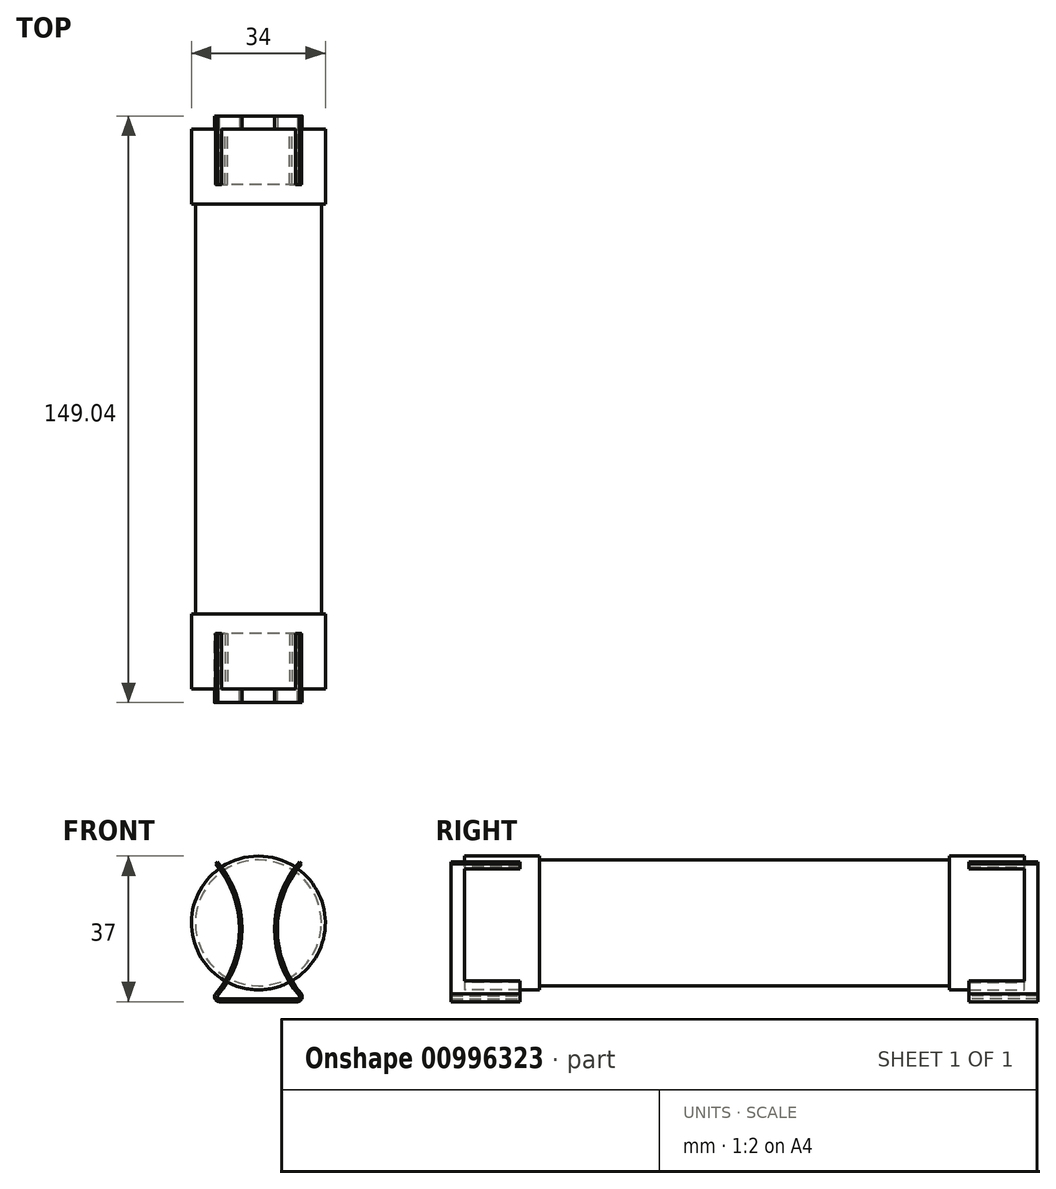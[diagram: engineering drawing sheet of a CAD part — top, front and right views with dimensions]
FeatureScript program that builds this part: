
annotation { "Feature Type Name" : "Feature", "Feature Type Description" : "" }
export const myFeature = defineFeature(function(context is Context, id is Id, definition is map)
    precondition{}
    {
        {
            var Q0;
            Q0=qCreatedBy(makeId("Front.planeOp"),FACE);
            var sketch = newSketch(context, id + "F0", { "sketchPlane" : qUnion([Q0])});
            skArc(sketch, "E0", {"start": v(-19.83, 17) * mm, "mid": v(-26.12, 0) * mm, "end": v(-19.83, -17) * mm});
            skArc(sketch, "E1", {"start": v(-19.3, 16.5) * mm, "mid": v(-25.4, 0) * mm, "end": v(-19.3, -16.5) * mm});
            skLineSegment(sketch, "E2", {"start": v(0, 0) * mm, "end": v(-25.4, 0) * mm, "construction": true});
            skLineSegment(sketch, "E3", {"start": v(-25.4, 0) * mm, "end": v(-19.3, 16.5) * mm, "construction": true});
            skLineSegment(sketch, "E4.MirrorCS", {"start": v(-25.4, 0) * mm, "end": v(-19.3, -16.5) * mm, "construction": true});
            skPoint(sketch, "E5", {"position": v(-26.12, 0) * mm});
            skLineSegment(sketch, "E6", {"start": v(-26.12, 0) * mm, "end": v(-19.83, 17) * mm, "construction": true});
            skLineSegment(sketch, "E7.MirrorCS", {"start": v(-26.12, 0) * mm, "end": v(-19.83, -17) * mm, "construction": true});
            skLineSegment(sketch, "E8", {"start": v(-19.83, -17) * mm, "end": v(-19.3, -16.5) * mm});
            skLineSegment(sketch, "E9", {"start": v(-19.83, 17) * mm, "end": v(-19.3, 16.5) * mm});
            skArc(sketch, "E10.filletArc", {"start": v(-20.29, -17.7) * mm, "mid": v(-19.87, -17.47) * mm, "end": v(-19.83, -17) * mm});
            skArc(sketch, "E11", {"start": v(-20.29, -18.47) * mm, "mid": v(-19.21, -17.78) * mm, "end": v(-19.3, -16.5) * mm});
            skLineSegment(sketch, "E12", {"start": v(-20.29, -17.7) * mm, "end": v(-40.18, -17.7) * mm});
            skLineSegment(sketch, "E13", {"start": v(-20.29, -18.47) * mm, "end": v(-40.18, -18.47) * mm});
            skLineSegment(sketch, "E14", {"start": v(-40.18, -18.47) * mm, "end": v(-40.18, -17.7) * mm});
            skLineSegment(sketch, "E15", {"start": v(-30.23, -17.7) * mm, "end": v(-30.23, -16.44) * mm, "construction": true});
            skLineSegment(sketch, "E16.MirrorCS", {"start": v(-40.63, -17) * mm, "end": v(-41.16, -16.5) * mm});
            skArc(sketch, "E17.MirrorCS", {"start": v(-40.18, -18.47) * mm, "mid": v(-41.25, -17.78) * mm, "end": v(-41.16, -16.5) * mm});
            skArc(sketch, "E18.MirrorCS", {"start": v(-40.18, -17.7) * mm, "mid": v(-40.6, -17.47) * mm, "end": v(-40.63, -17) * mm});
            skLineSegment(sketch, "E19.MirrorCS", {"start": v(-40.63, 17) * mm, "end": v(-41.16, 16.5) * mm});
            skLineSegment(sketch, "E20.MirrorCS", {"start": v(-34.35, 0) * mm, "end": v(-40.63, -17) * mm, "construction": true});
            skLineSegment(sketch, "E21.MirrorCS", {"start": v(-35.07, 0) * mm, "end": v(-41.16, 16.5) * mm, "construction": true});
            skArc(sketch, "E22.MirrorCS", {"start": v(-40.63, 17) * mm, "mid": v(-34.35, 0) * mm, "end": v(-40.63, -17) * mm});
            skLineSegment(sketch, "E23.MirrorCS", {"start": v(-35.07, 0) * mm, "end": v(-41.16, -16.5) * mm, "construction": true});
            skArc(sketch, "E24.MirrorCS", {"start": v(-41.16, 16.5) * mm, "mid": v(-35.07, 0) * mm, "end": v(-41.16, -16.5) * mm});
            skLineSegment(sketch, "E25.MirrorCS", {"start": v(-34.35, 0) * mm, "end": v(-40.63, 17) * mm, "construction": true});
            skPoint(sketch, "E26.MirrorP", {"position": v(-34.35, 0) * mm});
            skSolve(sketch);
        }
        {
            var Q0;
            Q0 = qSketchRegion(id + "F0", true);
            extrude(context, id + "F1", {"entities" : qUnion([Q0]), "depth" : 17.5 * mm, "offsetDistance" : 25 * mm});
        }
        {
            var Q0;
            Q0=qCreatedBy(makeId("Front.planeOp"),FACE);
            cPlane(context, id + "F2", {"entities" : qUnion([Q0]), "cplaneType" : CPlaneType.OFFSET, "offset" : 14.1 * mm, "width" : 150 * mm, "height" : 150 * mm});
        }
        {
            var Q0;
            Q0=qCreatedBy(id+"F2.planeOp",FACE);
            var sketch = newSketch(context, id + "F3", { "sketchPlane" : qUnion([Q0])});
            skCircle(sketch, "E27", {"center": v(-30.23, 1.53) * mm, "radius": 17 * mm});
            skLineSegment(sketch, "E28.0", {"start": v(-20.29, -17.7) * mm, "end": v(-40.18, -17.7) * mm});
            skPoint(sketch, "E29.0", {"position": v(-30.23, -18.47) * mm});
            skLineSegment(sketch, "E30", {"start": v(-30.23, -18.47) * mm, "end": v(-30.23, 1.53) * mm, "construction": true});
            skSolve(sketch);
        }
        {
            var Q0;
            Q0=makeQuery(id+"F3.imprint","IMPRINT",FACE,{"disambiguationData":[TD([[makeQuery(id+"F3.imprint","IMPRINT",EDGE,{"derivedFrom":sQuery(id+"F3.wireOp",EDGE,"E27")}),1.0]])]});
            extrude(context, id + "F4", {"entities" : qUnion([Q0]), "operationType" : NewBodyOperationType.ADD, "oppositeDirection" : true, "depth" : 19.05 * mm, "offsetDistance" : 25 * mm});
        }
        {
            var Q0;
            Q0=makeQuery(id+"F4.opExtrude","CAP_FACE",FACE,{"disambiguationData":[OSD([sQuery(id+"F3.wireOp",EDGE,"E27")])],"isStart":false});
            var sketch = newSketch(context, id + "F5", { "sketchPlane" : qUnion([Q0])});
            skCircle(sketch, "E31", {"center": v(30.23, 1.53) * mm, "radius": 16 * mm});
            skSolve(sketch);
        }
        {
            var Q0;
            Q0 = qSketchRegion(id + "F5", true);
            extrude(context, id + "F6", {"entities" : qUnion([Q0]), "operationType" : NewBodyOperationType.ADD, "depth" : 52.07 * mm, "offsetDistance" : 25 * mm});
        }
        {
            var Q0;
            Q0=qCreatedBy(id+"F2.planeOp",FACE);
            cPlane(context, id + "F7", {"entities" : qUnion([Q0]), "cplaneType" : CPlaneType.OFFSET, "offset" : 71.12 * mm, "oppositeDirection" : true, "width" : 150 * mm, "height" : 150 * mm});
        }
        {
            var Q0;
            Q0=makeQuery(id+"F1.opExtrude","SWEPT_BODY",BODY,{"disambiguationData":[OSD([sQuery(id+"F0.wireOp",EDGE,"E0"),sQuery(id+"F0.wireOp",EDGE,"E1"),sQuery(id+"F0.wireOp",EDGE,"E9"),sQuery(id+"F0.wireOp",EDGE,"E10.filletArc"),sQuery(id+"F0.wireOp",EDGE,"E11"),sQuery(id+"F0.wireOp",EDGE,"E12"),sQuery(id+"F0.wireOp",EDGE,"E13"),sQuery(id+"F0.wireOp",EDGE,"E17.MirrorCS"),sQuery(id+"F0.wireOp",EDGE,"E18.MirrorCS"),sQuery(id+"F0.wireOp",EDGE,"E19.MirrorCS"),sQuery(id+"F0.wireOp",EDGE,"E22.MirrorCS"),sQuery(id+"F0.wireOp",EDGE,"E24.MirrorCS")])]});
            var Q1;
            Q1=qCreatedBy(id+"F7.planeOp",FACE);
            mirror(context, id + "F8", {"operationType" : NewBodyOperationType.ADD, "entities" : qUnion([Q0]), "mirrorPlane" : qUnion([Q1])});
        }
    });
